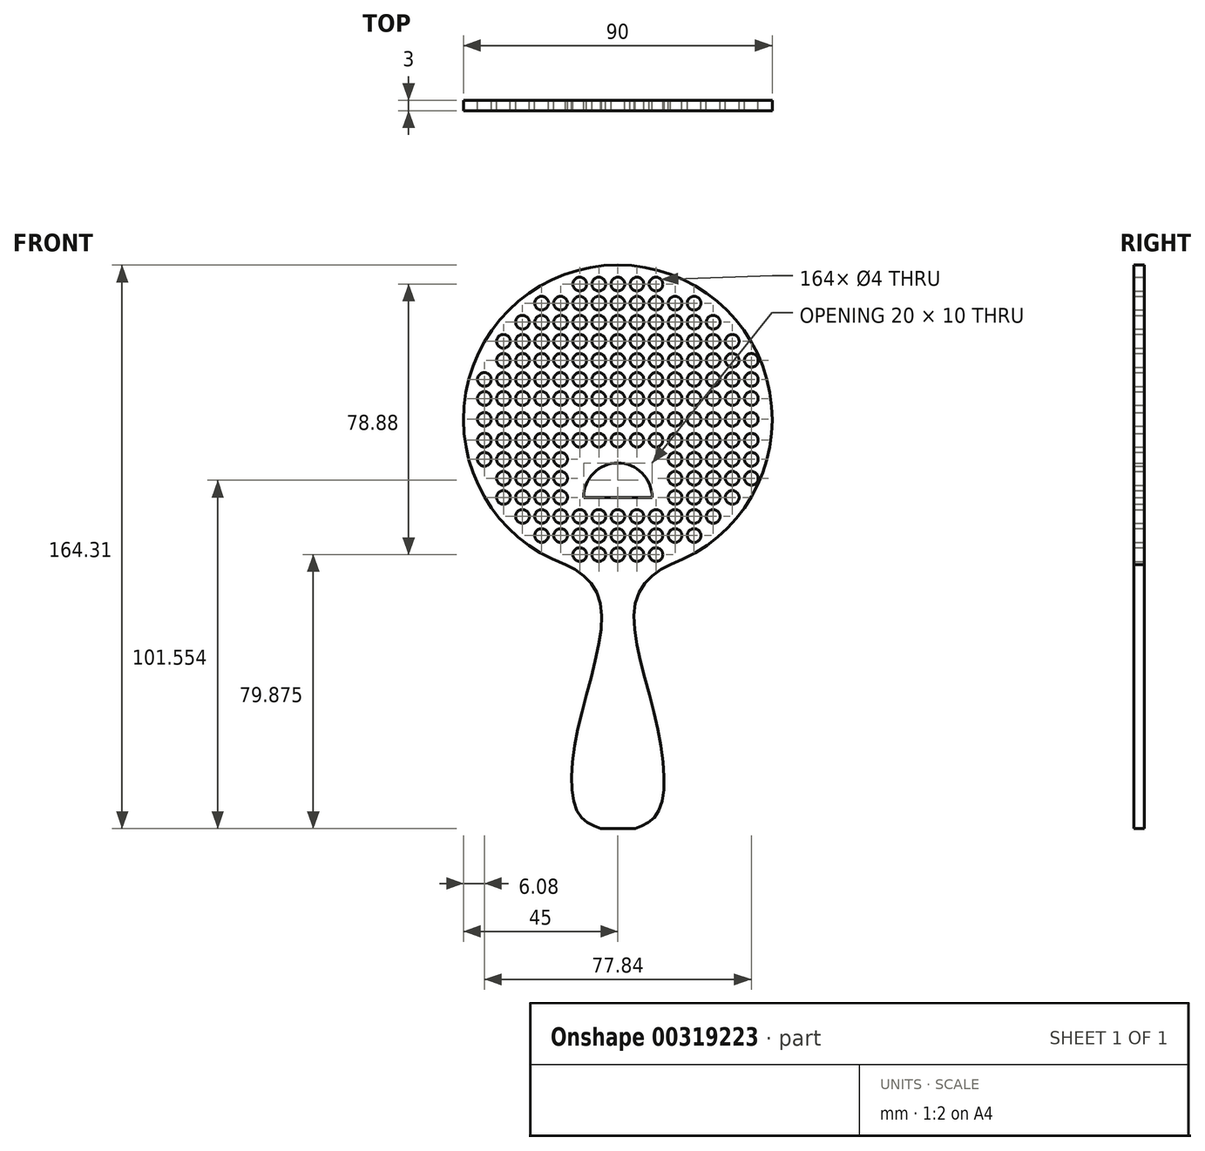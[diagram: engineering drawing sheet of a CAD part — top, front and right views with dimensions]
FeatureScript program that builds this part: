
annotation { "Feature Type Name" : "Feature", "Feature Type Description" : "" }
export const myFeature = defineFeature(function(context is Context, id is Id, definition is map)
    precondition{}
    {
        {
            var Q0;
            Q0=qCreatedBy(makeId("Front.planeOp"),FACE);
            var sketch = newSketch(context, id + "F0", { "sketchPlane" : qUnion([Q0])});
            skArc(sketch, "E0", {"start": v(15.33, 4.66) * mm, "mid": v(0, 91.96) * mm, "end": v(-15.33, 4.66) * mm});
            skLineSegment(sketch, "E1", {"start": v(0, 46.96) * mm, "end": v(45, 46.96) * mm, "construction": true});
            skCircle(sketch, "E2", {"center": v(-11.12, 86.4) * mm, "radius": 2 * mm});
            skCircle(sketch, "E3", {"center": v(-11.12, 80.85) * mm, "radius": 2 * mm});
            skCircle(sketch, "E4", {"center": v(-5.56, 86.4) * mm, "radius": 2 * mm});
            skCircle(sketch, "E5", {"center": v(-16.68, 80.85) * mm, "radius": 2 * mm});
            skCircle(sketch, "E6", {"center": v(0, 86.4) * mm, "radius": 2 * mm});
            skCircle(sketch, "E7", {"center": v(5.56, 86.4) * mm, "radius": 2 * mm});
            skCircle(sketch, "E8", {"center": v(11.12, 86.4) * mm, "radius": 2 * mm});
            skCircle(sketch, "E9", {"center": v(-5.56, 80.85) * mm, "radius": 2 * mm});
            skCircle(sketch, "E10", {"center": v(0, 80.85) * mm, "radius": 2 * mm});
            skCircle(sketch, "E11", {"center": v(5.56, 80.85) * mm, "radius": 2 * mm});
            skCircle(sketch, "E12", {"center": v(11.12, 80.85) * mm, "radius": 2 * mm});
            skCircle(sketch, "E13", {"center": v(16.68, 80.85) * mm, "radius": 2 * mm});
            skCircle(sketch, "E14", {"center": v(22.24, 80.85) * mm, "radius": 2 * mm});
            skCircle(sketch, "E15", {"center": v(-22.24, 80.85) * mm, "radius": 2 * mm});
            skCircle(sketch, "E16", {"center": v(-27.8, 75.29) * mm, "radius": 2 * mm});
            skCircle(sketch, "E17.1.0.0", {"center": v(-22.24, 75.29) * mm, "radius": 2 * mm});
            skCircle(sketch, "E17.2.0.0", {"center": v(-16.68, 75.29) * mm, "radius": 2 * mm});
            skCircle(sketch, "E17.3.0.0", {"center": v(-11.12, 75.29) * mm, "radius": 2 * mm});
            skCircle(sketch, "E17.4.0.0", {"center": v(-5.56, 75.29) * mm, "radius": 2 * mm});
            skCircle(sketch, "E17.5.0.0", {"center": v(0, 75.29) * mm, "radius": 2 * mm});
            skCircle(sketch, "E17.6.0.0", {"center": v(5.56, 75.29) * mm, "radius": 2 * mm});
            skCircle(sketch, "E17.7.0.0", {"center": v(11.12, 75.29) * mm, "radius": 2 * mm});
            skCircle(sketch, "E17.8.0.0", {"center": v(16.68, 75.29) * mm, "radius": 2 * mm});
            skCircle(sketch, "E17.9.0.0", {"center": v(22.24, 75.29) * mm, "radius": 2 * mm});
            skCircle(sketch, "E17.10.0.0", {"center": v(27.8, 75.29) * mm, "radius": 2 * mm});
            skLineSegment(sketch, "E17.direction1", {"start": v(-27.8, 75.29) * mm, "end": v(-22.24, 75.29) * mm, "construction": true});
            skCircle(sketch, "E18", {"center": v(-33.36, 69.73) * mm, "radius": 2 * mm});
            skCircle(sketch, "E19.1.0.0", {"center": v(-27.8, 69.73) * mm, "radius": 2 * mm});
            skCircle(sketch, "E19.2.0.0", {"center": v(-22.24, 69.73) * mm, "radius": 2 * mm});
            skCircle(sketch, "E19.3.0.0", {"center": v(-16.68, 69.73) * mm, "radius": 2 * mm});
            skCircle(sketch, "E19.4.0.0", {"center": v(-11.12, 69.73) * mm, "radius": 2 * mm});
            skCircle(sketch, "E19.5.0.0", {"center": v(-5.56, 69.73) * mm, "radius": 2 * mm});
            skCircle(sketch, "E19.6.0.0", {"center": v(0, 69.73) * mm, "radius": 2 * mm});
            skCircle(sketch, "E19.7.0.0", {"center": v(5.56, 69.73) * mm, "radius": 2 * mm});
            skCircle(sketch, "E19.8.0.0", {"center": v(11.12, 69.73) * mm, "radius": 2 * mm});
            skCircle(sketch, "E19.9.0.0", {"center": v(16.68, 69.73) * mm, "radius": 2 * mm});
            skCircle(sketch, "E19.10.0.0", {"center": v(22.24, 69.73) * mm, "radius": 2 * mm});
            skCircle(sketch, "E19.11.0.0", {"center": v(27.8, 69.73) * mm, "radius": 2 * mm});
            skCircle(sketch, "E19.12.0.0", {"center": v(33.36, 69.73) * mm, "radius": 2 * mm});
            skLineSegment(sketch, "E19.direction1", {"start": v(-33.36, 69.73) * mm, "end": v(-27.8, 69.73) * mm, "construction": true});
            skCircle(sketch, "E20", {"center": v(-33.36, 64.17) * mm, "radius": 2 * mm});
            skCircle(sketch, "E21", {"center": v(-38.92, 58.6) * mm, "radius": 2 * mm});
            skCircle(sketch, "E22", {"center": v(-38.92, 53.05) * mm, "radius": 2 * mm});
            skCircle(sketch, "E23", {"center": v(-38.92, 46.96) * mm, "radius": 2 * mm});
            skCircle(sketch, "E24.1.0.0", {"center": v(-27.8, 64.17) * mm, "radius": 2 * mm});
            skCircle(sketch, "E24.1.0.1", {"center": v(-33.36, 58.6) * mm, "radius": 2 * mm});
            skCircle(sketch, "E24.1.0.2", {"center": v(-33.36, 53.05) * mm, "radius": 2 * mm});
            skCircle(sketch, "E24.1.0.3", {"center": v(-33.36, 46.96) * mm, "radius": 2 * mm});
            skCircle(sketch, "E24.2.0.0", {"center": v(-22.24, 64.17) * mm, "radius": 2 * mm});
            skCircle(sketch, "E24.2.0.1", {"center": v(-27.8, 58.6) * mm, "radius": 2 * mm});
            skCircle(sketch, "E24.2.0.2", {"center": v(-27.8, 53.05) * mm, "radius": 2 * mm});
            skCircle(sketch, "E24.2.0.3", {"center": v(-27.8, 46.96) * mm, "radius": 2 * mm});
            skCircle(sketch, "E24.3.0.0", {"center": v(-16.68, 64.17) * mm, "radius": 2 * mm});
            skCircle(sketch, "E24.3.0.1", {"center": v(-22.24, 58.6) * mm, "radius": 2 * mm});
            skCircle(sketch, "E24.3.0.2", {"center": v(-22.24, 53.05) * mm, "radius": 2 * mm});
            skCircle(sketch, "E24.3.0.3", {"center": v(-22.24, 46.96) * mm, "radius": 2 * mm});
            skCircle(sketch, "E24.4.0.0", {"center": v(-11.12, 64.17) * mm, "radius": 2 * mm});
            skCircle(sketch, "E24.4.0.1", {"center": v(-16.68, 58.6) * mm, "radius": 2 * mm});
            skCircle(sketch, "E24.4.0.2", {"center": v(-16.68, 53.05) * mm, "radius": 2 * mm});
            skCircle(sketch, "E24.4.0.3", {"center": v(-16.68, 46.96) * mm, "radius": 2 * mm});
            skCircle(sketch, "E24.5.0.0", {"center": v(-5.56, 64.17) * mm, "radius": 2 * mm});
            skCircle(sketch, "E24.5.0.1", {"center": v(-11.12, 58.6) * mm, "radius": 2 * mm});
            skCircle(sketch, "E24.5.0.2", {"center": v(-11.12, 53.05) * mm, "radius": 2 * mm});
            skCircle(sketch, "E24.5.0.3", {"center": v(-11.12, 46.96) * mm, "radius": 2 * mm});
            skCircle(sketch, "E24.6.0.0", {"center": v(0, 64.17) * mm, "radius": 2 * mm});
            skCircle(sketch, "E24.6.0.1", {"center": v(-5.56, 58.6) * mm, "radius": 2 * mm});
            skCircle(sketch, "E24.6.0.2", {"center": v(-5.56, 53.05) * mm, "radius": 2 * mm});
            skCircle(sketch, "E24.6.0.3", {"center": v(-5.56, 46.96) * mm, "radius": 2 * mm});
            skCircle(sketch, "E24.7.0.0", {"center": v(5.56, 64.17) * mm, "radius": 2 * mm});
            skCircle(sketch, "E24.7.0.1", {"center": v(0, 58.6) * mm, "radius": 2 * mm});
            skCircle(sketch, "E24.7.0.2", {"center": v(0, 53.05) * mm, "radius": 2 * mm});
            skCircle(sketch, "E24.7.0.3", {"center": v(0, 46.96) * mm, "radius": 2 * mm});
            skCircle(sketch, "E24.8.0.0", {"center": v(11.12, 64.17) * mm, "radius": 2 * mm});
            skCircle(sketch, "E24.8.0.1", {"center": v(5.56, 58.6) * mm, "radius": 2 * mm});
            skCircle(sketch, "E24.8.0.2", {"center": v(5.56, 53.05) * mm, "radius": 2 * mm});
            skCircle(sketch, "E24.8.0.3", {"center": v(5.56, 46.96) * mm, "radius": 2 * mm});
            skCircle(sketch, "E24.9.0.0", {"center": v(16.68, 64.17) * mm, "radius": 2 * mm});
            skCircle(sketch, "E24.9.0.1", {"center": v(11.12, 58.6) * mm, "radius": 2 * mm});
            skCircle(sketch, "E24.9.0.2", {"center": v(11.12, 53.05) * mm, "radius": 2 * mm});
            skCircle(sketch, "E24.9.0.3", {"center": v(11.12, 46.96) * mm, "radius": 2 * mm});
            skCircle(sketch, "E24.10.0.0", {"center": v(22.24, 64.17) * mm, "radius": 2 * mm});
            skCircle(sketch, "E24.10.0.1", {"center": v(16.68, 58.6) * mm, "radius": 2 * mm});
            skCircle(sketch, "E24.10.0.2", {"center": v(16.68, 53.05) * mm, "radius": 2 * mm});
            skCircle(sketch, "E24.10.0.3", {"center": v(16.68, 46.96) * mm, "radius": 2 * mm});
            skCircle(sketch, "E24.11.0.0", {"center": v(27.8, 64.17) * mm, "radius": 2 * mm});
            skCircle(sketch, "E24.11.0.1", {"center": v(22.24, 58.6) * mm, "radius": 2 * mm});
            skCircle(sketch, "E24.11.0.2", {"center": v(22.24, 53.05) * mm, "radius": 2 * mm});
            skCircle(sketch, "E24.11.0.3", {"center": v(22.24, 46.96) * mm, "radius": 2 * mm});
            skCircle(sketch, "E24.12.0.0", {"center": v(33.36, 64.17) * mm, "radius": 2 * mm});
            skCircle(sketch, "E24.12.0.1", {"center": v(27.8, 58.6) * mm, "radius": 2 * mm});
            skCircle(sketch, "E24.12.0.2", {"center": v(27.8, 53.05) * mm, "radius": 2 * mm});
            skCircle(sketch, "E24.12.0.3", {"center": v(27.8, 46.96) * mm, "radius": 2 * mm});
            skCircle(sketch, "E24.13.0.0", {"center": v(38.92, 64.17) * mm, "radius": 2 * mm});
            skCircle(sketch, "E24.13.0.1", {"center": v(33.36, 58.6) * mm, "radius": 2 * mm});
            skCircle(sketch, "E24.13.0.2", {"center": v(33.36, 53.05) * mm, "radius": 2 * mm});
            skCircle(sketch, "E24.13.0.3", {"center": v(33.36, 46.96) * mm, "radius": 2 * mm});
            skCircle(sketch, "E24.14.0.1", {"center": v(38.92, 58.6) * mm, "radius": 2 * mm});
            skCircle(sketch, "E24.14.0.2", {"center": v(38.92, 53.05) * mm, "radius": 2 * mm});
            skCircle(sketch, "E24.14.0.3", {"center": v(38.92, 46.96) * mm, "radius": 2 * mm});
            skLineSegment(sketch, "E24.direction1", {"start": v(-38.92, 46.96) * mm, "end": v(-33.36, 46.96) * mm, "construction": true});
            skLineSegment(sketch, "E25.MirrorCS", {"start": v(-27.8, 18.64) * mm, "end": v(-22.24, 18.64) * mm, "construction": true});
            skCircle(sketch, "E26.MirrorC", {"center": v(-38.92, 35.32) * mm, "radius": 2 * mm});
            skCircle(sketch, "E27.MirrorC", {"center": v(5.56, 13.08) * mm, "radius": 2 * mm});
            skCircle(sketch, "E28.MirrorC", {"center": v(27.8, 35.32) * mm, "radius": 2 * mm});
            skCircle(sketch, "E29.MirrorC", {"center": v(-16.68, 35.32) * mm, "radius": 2 * mm});
            skCircle(sketch, "E30.MirrorC", {"center": v(-38.92, 40.88) * mm, "radius": 2 * mm});
            skCircle(sketch, "E31.MirrorC", {"center": v(-33.36, 24.2) * mm, "radius": 2 * mm});
            skCircle(sketch, "E32.MirrorC", {"center": v(11.12, 13.08) * mm, "radius": 2 * mm});
            skCircle(sketch, "E33.MirrorC", {"center": v(27.8, 40.88) * mm, "radius": 2 * mm});
            skCircle(sketch, "E34.MirrorC", {"center": v(5.56, 40.88) * mm, "radius": 2 * mm});
            skCircle(sketch, "E35.MirrorC", {"center": v(-16.68, 40.88) * mm, "radius": 2 * mm});
            skCircle(sketch, "E36.MirrorC", {"center": v(-27.8, 24.2) * mm, "radius": 2 * mm});
            skCircle(sketch, "E37.MirrorC", {"center": v(16.68, 13.08) * mm, "radius": 2 * mm});
            skCircle(sketch, "E38.MirrorC", {"center": v(-27.8, 29.76) * mm, "radius": 2 * mm});
            skCircle(sketch, "E39.MirrorC", {"center": v(-22.24, 24.2) * mm, "radius": 2 * mm});
            skCircle(sketch, "E40.MirrorC", {"center": v(22.24, 13.08) * mm, "radius": 2 * mm});
            skCircle(sketch, "E41.MirrorC", {"center": v(38.92, 29.76) * mm, "radius": 2 * mm});
            skCircle(sketch, "E42.MirrorC", {"center": v(16.68, 29.76) * mm, "radius": 2 * mm});
            skCircle(sketch, "E43.MirrorC", {"center": v(-22.24, 13.08) * mm, "radius": 2 * mm});
            skCircle(sketch, "E44.MirrorC", {"center": v(-33.36, 35.32) * mm, "radius": 2 * mm});
            skCircle(sketch, "E45.MirrorC", {"center": v(-16.68, 24.2) * mm, "radius": 2 * mm});
            skCircle(sketch, "E46.MirrorC", {"center": v(33.36, 35.32) * mm, "radius": 2 * mm});
            skCircle(sketch, "E47.MirrorC", {"center": v(-27.8, 18.64) * mm, "radius": 2 * mm});
            skCircle(sketch, "E48.MirrorC", {"center": v(11.12, 40.88) * mm, "radius": 2 * mm});
            skCircle(sketch, "E49.MirrorC", {"center": v(-11.12, 40.88) * mm, "radius": 2 * mm});
            skCircle(sketch, "E50.MirrorC", {"center": v(-33.36, 40.88) * mm, "radius": 2 * mm});
            skCircle(sketch, "E51.MirrorC", {"center": v(33.36, 40.88) * mm, "radius": 2 * mm});
            skCircle(sketch, "E52.MirrorC", {"center": v(-22.24, 18.64) * mm, "radius": 2 * mm});
            skCircle(sketch, "E53.MirrorC", {"center": v(22.24, 24.2) * mm, "radius": 2 * mm});
            skCircle(sketch, "E54.MirrorC", {"center": v(5.56, 18.64) * mm, "radius": 2 * mm});
            skCircle(sketch, "E55.MirrorC", {"center": v(33.36, 29.76) * mm, "radius": 2 * mm});
            skCircle(sketch, "E56.MirrorC", {"center": v(-27.8, 40.88) * mm, "radius": 2 * mm});
            skCircle(sketch, "E57.MirrorC", {"center": v(-5.56, 40.88) * mm, "radius": 2 * mm});
            skCircle(sketch, "E58.MirrorC", {"center": v(16.68, 40.88) * mm, "radius": 2 * mm});
            skCircle(sketch, "E59.MirrorC", {"center": v(-5.56, 7.52) * mm, "radius": 2 * mm});
            skCircle(sketch, "E60.MirrorC", {"center": v(0, 13.08) * mm, "radius": 2 * mm});
            skCircle(sketch, "E61.MirrorC", {"center": v(-5.56, 18.64) * mm, "radius": 2 * mm});
            skCircle(sketch, "E62.MirrorC", {"center": v(27.8, 18.64) * mm, "radius": 2 * mm});
            skCircle(sketch, "E63.MirrorC", {"center": v(-33.36, 29.76) * mm, "radius": 2 * mm});
            skCircle(sketch, "E64.MirrorC", {"center": v(0, 7.52) * mm, "radius": 2 * mm});
            skCircle(sketch, "E65.MirrorC", {"center": v(38.92, 40.88) * mm, "radius": 2 * mm});
            skCircle(sketch, "E66.MirrorC", {"center": v(-27.8, 35.32) * mm, "radius": 2 * mm});
            skCircle(sketch, "E67.MirrorC", {"center": v(16.68, 35.32) * mm, "radius": 2 * mm});
            skCircle(sketch, "E68.MirrorC", {"center": v(22.24, 18.64) * mm, "radius": 2 * mm});
            skCircle(sketch, "E69.MirrorC", {"center": v(-16.68, 18.64) * mm, "radius": 2 * mm});
            skCircle(sketch, "E70.MirrorC", {"center": v(27.8, 29.76) * mm, "radius": 2 * mm});
            skCircle(sketch, "E71.MirrorC", {"center": v(-11.12, 7.52) * mm, "radius": 2 * mm});
            skCircle(sketch, "E72.MirrorC", {"center": v(16.68, 24.2) * mm, "radius": 2 * mm});
            skCircle(sketch, "E73.MirrorC", {"center": v(-11.12, 13.08) * mm, "radius": 2 * mm});
            skCircle(sketch, "E74.MirrorC", {"center": v(-11.12, 18.64) * mm, "radius": 2 * mm});
            skCircle(sketch, "E75.MirrorC", {"center": v(-5.56, 13.08) * mm, "radius": 2 * mm});
            skLineSegment(sketch, "E76.MirrorCS", {"start": v(-33.36, 24.2) * mm, "end": v(-27.8, 24.2) * mm, "construction": true});
            skCircle(sketch, "E77.MirrorC", {"center": v(-16.68, 29.76) * mm, "radius": 2 * mm});
            skCircle(sketch, "E78.MirrorC", {"center": v(-16.68, 13.08) * mm, "radius": 2 * mm});
            skCircle(sketch, "E79.MirrorC", {"center": v(33.36, 24.2) * mm, "radius": 2 * mm});
            skCircle(sketch, "E80.MirrorC", {"center": v(-22.24, 40.88) * mm, "radius": 2 * mm});
            skCircle(sketch, "E81.MirrorC", {"center": v(0, 18.64) * mm, "radius": 2 * mm});
            skCircle(sketch, "E82.MirrorC", {"center": v(16.68, 18.64) * mm, "radius": 2 * mm});
            skCircle(sketch, "E83.MirrorC", {"center": v(22.24, 40.88) * mm, "radius": 2 * mm});
            skCircle(sketch, "E84.MirrorC", {"center": v(11.12, 7.52) * mm, "radius": 2 * mm});
            skCircle(sketch, "E85.MirrorC", {"center": v(22.24, 29.76) * mm, "radius": 2 * mm});
            skCircle(sketch, "E86.MirrorC", {"center": v(-22.24, 35.32) * mm, "radius": 2 * mm});
            skCircle(sketch, "E87.MirrorC", {"center": v(-22.24, 29.76) * mm, "radius": 2 * mm});
            skCircle(sketch, "E88.MirrorC", {"center": v(0, 40.88) * mm, "radius": 2 * mm});
            skCircle(sketch, "E89.MirrorC", {"center": v(5.56, 7.52) * mm, "radius": 2 * mm});
            skCircle(sketch, "E90.MirrorC", {"center": v(27.8, 24.2) * mm, "radius": 2 * mm});
            skCircle(sketch, "E91.MirrorC", {"center": v(22.24, 35.32) * mm, "radius": 2 * mm});
            skCircle(sketch, "E92.MirrorC", {"center": v(38.92, 35.32) * mm, "radius": 2 * mm});
            skCircle(sketch, "E93.MirrorC", {"center": v(11.12, 18.64) * mm, "radius": 2 * mm});
            skLineSegment(sketch, "E94", {"start": v(0, 24.2) * mm, "end": v(-10, 24.2) * mm, "construction": true});
            skLineSegment(sketch, "E95", {"start": v(0, 24.2) * mm, "end": v(10, 24.2) * mm, "construction": true});
            skArc(sketch, "E96", {"start": v(10, 24.2) * mm, "mid": v(0, 34.2) * mm, "end": v(-10, 24.2) * mm});
            skLineSegment(sketch, "E97", {"start": v(-10, 24.2) * mm, "end": v(10, 24.2) * mm});
            skLineSegment(sketch, "E98", {"start": v(4.71, -9.5) * mm, "end": v(5, -9.5) * mm, "construction": true});
            skLineSegment(sketch, "E99", {"start": v(5, -1.55) * mm, "end": v(5, -74.74) * mm, "construction": true});
            skLineSegment(sketch, "E100.MirrorCS", {"start": v(-5, -1.55) * mm, "end": v(-5, -74.74) * mm, "construction": true});
            skFitSpline(sketch, "E101", {"points": [v(-15.33, 4.66) * mm, v(-5, -7.05) * mm, v(-11.6, -43.12) * mm, v(-11.49, -68.01) * mm, v(-5, -72.35) * mm], "startDerivative": vector(67.65, -30.97) * mm, "endDerivative": vector(43.9, -17.61) * mm});
            skLineSegment(sketch, "E102", {"start": v(-5, -72.35) * mm, "end": v(0, -72.35) * mm});
            skFitSpline(sketch, "E103.MirrorCS", {"points": [v(15.33, 4.66) * mm, v(5, -7.05) * mm, v(11.6, -43.12) * mm, v(11.49, -68.01) * mm, v(5, -72.35) * mm], "startDerivative": vector(-67.65, -30.97) * mm, "endDerivative": vector(-43.9, -17.61) * mm});
            skLineSegment(sketch, "E104.MirrorCS", {"start": v(5, -72.35) * mm, "end": v(0, -72.35) * mm});
            skPoint(sketch, "E105.orphan", {"position": v(0, -9.5) * mm});
            skLineSegment(sketch, "E106", {"start": v(-5, -1.55) * mm, "end": v(5, -1.55) * mm, "construction": true});
            skPoint(sketch, "E107", {"position": v(0, -1.55) * mm});
            skSolve(sketch);
        }
        {
            var Q0;
            Q0=makeQuery(id+"F0.imprint","IMPRINT",FACE,{"disambiguationData":[TD([[makeQuery(id+"F0.imprint","IMPRINT",EDGE,{"derivedFrom":sQuery(id+"F0.wireOp",EDGE,"E0")}),1.0]])]});
            extrude(context, id + "F1", {"entities" : qUnion([Q0]), "endBound" : BoundingType.SYMMETRIC, "depth" : 3 * mm});
        }
    });
